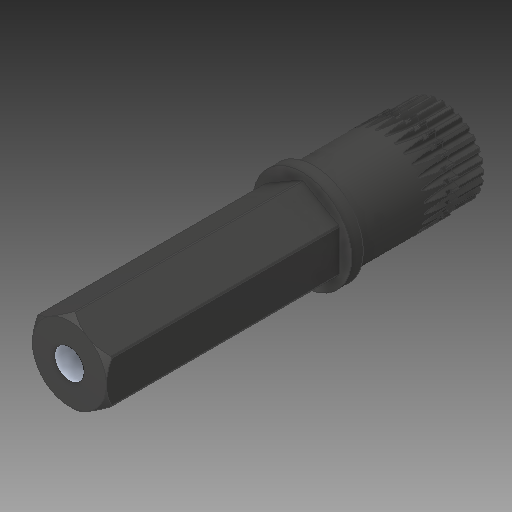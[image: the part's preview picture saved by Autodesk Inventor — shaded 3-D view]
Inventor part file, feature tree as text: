
AUTODESK INVENTOR PART (.ipt)
format: ipt  version: 2017 (Build 210142000, 142)  size: 1,432,576 bytes
history: native  units: in
note: dims shown in document units (in); Inventor stores cm internally (conversion verified against a paired STEP export)
features: fillet x1
ambient origin geometry x8: Origin, YZ Plane, XZ Plane, XY Plane, X Axis, Y Axis, Z Axis, Center Point
bodies: Solid1 (feature_tree)
feature tree (1):
  fillet  "Fillet5"  [1 undecoded]
note: 1 required parameter value undecoded (feature->parameter linkage not recoverable at this tier; creation-order binding heuristic only, values carry confidence <= 0.55)
